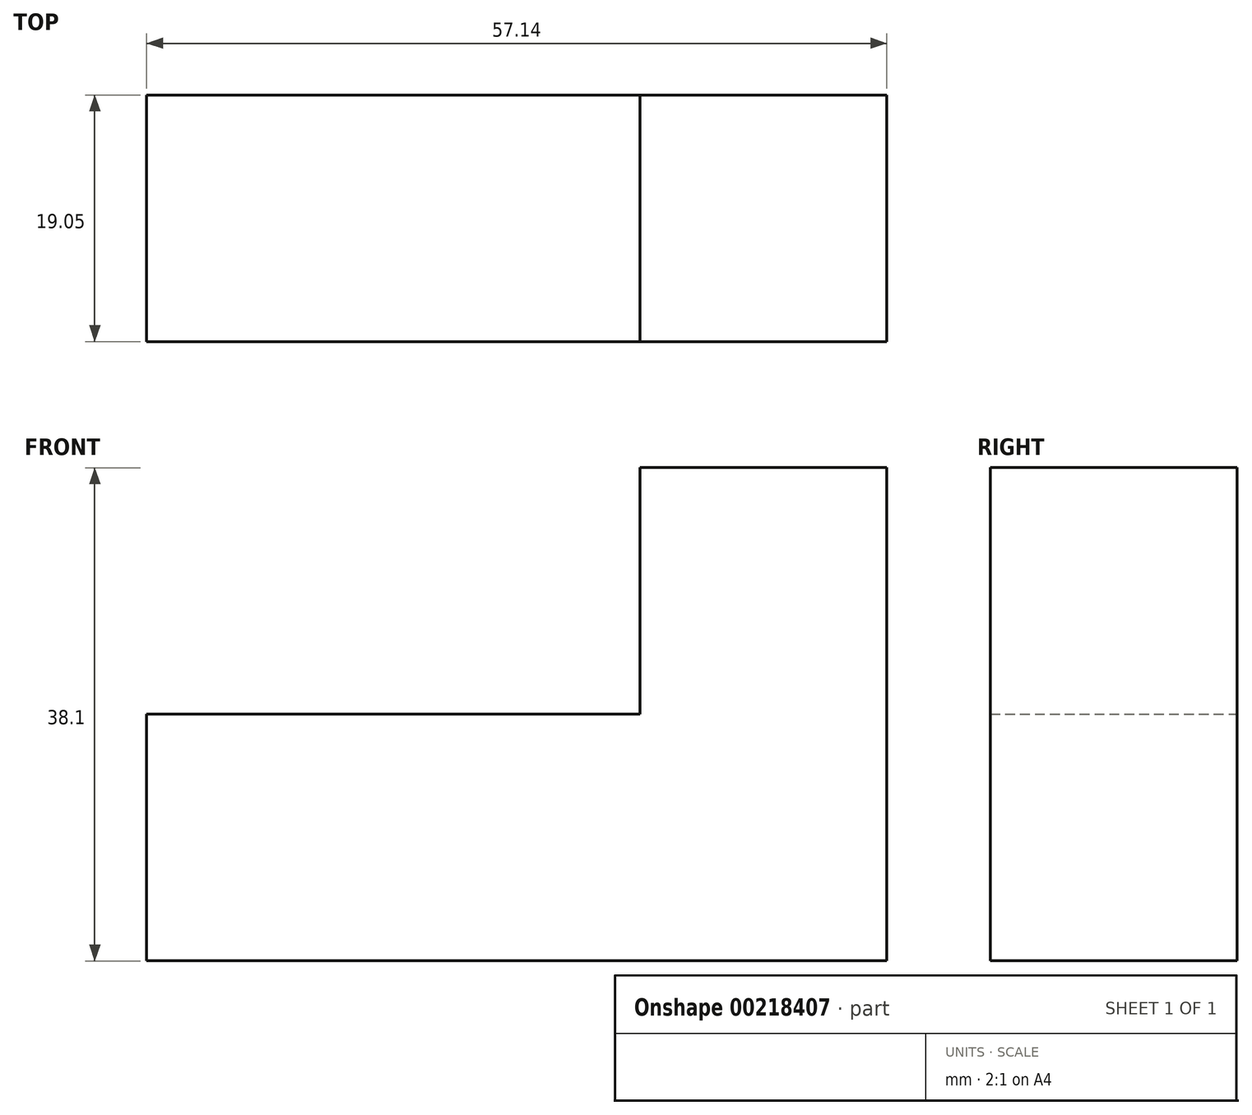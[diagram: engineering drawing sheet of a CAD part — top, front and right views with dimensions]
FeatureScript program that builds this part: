
annotation { "Feature Type Name" : "Feature", "Feature Type Description" : "" }
export const myFeature = defineFeature(function(context is Context, id is Id, definition is map)
    precondition{}
    {
        {
            var Q0;
            Q0=qCreatedBy(makeId("Front.planeOp"),FACE);
            var sketch = newSketch(context, id + "F0", { "sketchPlane" : qUnion([Q0])});
            skLineSegment(sketch, "E0.bottom", {"start": v(9.52, 9.53) * mm, "end": v(-9.53, 9.53) * mm});
            skLineSegment(sketch, "E0.top", {"start": v(9.53, -9.53) * mm, "end": v(-9.52, -9.53) * mm});
            skLineSegment(sketch, "E0.left", {"start": v(9.52, 9.53) * mm, "end": v(9.53, -9.52) * mm});
            skLineSegment(sketch, "E0.right", {"start": v(-9.53, 9.53) * mm, "end": v(-9.52, -9.53) * mm});
            skPoint(sketch, "E0.middle", {"position": v(0, 0) * mm});
            skLineSegment(sketch, "E1", {"start": v(-9.53, 9.53) * mm, "end": v(-28.58, 9.52) * mm});
            skLineSegment(sketch, "E2", {"start": v(-28.58, 9.52) * mm, "end": v(-28.58, -9.53) * mm});
            skLineSegment(sketch, "E3", {"start": v(-28.58, -9.53) * mm, "end": v(-9.52, -9.53) * mm});
            skLineSegment(sketch, "E4", {"start": v(9.52, 9.53) * mm, "end": v(28.57, 9.53) * mm});
            skLineSegment(sketch, "E5", {"start": v(28.57, 9.53) * mm, "end": v(28.57, -9.53) * mm});
            skLineSegment(sketch, "E6", {"start": v(28.57, -9.53) * mm, "end": v(9.53, -9.53) * mm});
            skLineSegment(sketch, "E7", {"start": v(9.52, 9.53) * mm, "end": v(9.52, 28.58) * mm});
            skLineSegment(sketch, "E8", {"start": v(9.52, 28.58) * mm, "end": v(28.57, 28.58) * mm});
            skLineSegment(sketch, "E9", {"start": v(28.57, 28.58) * mm, "end": v(28.57, 9.53) * mm});
            skSolve(sketch);
        }
        {
            var Q0;
            Q0 = qSketchRegion(id + "F0", true);
            extrude(context, id + "F1", {"entities" : qUnion([Q0]), "depth" : 19.05 * mm});
        }
    });
